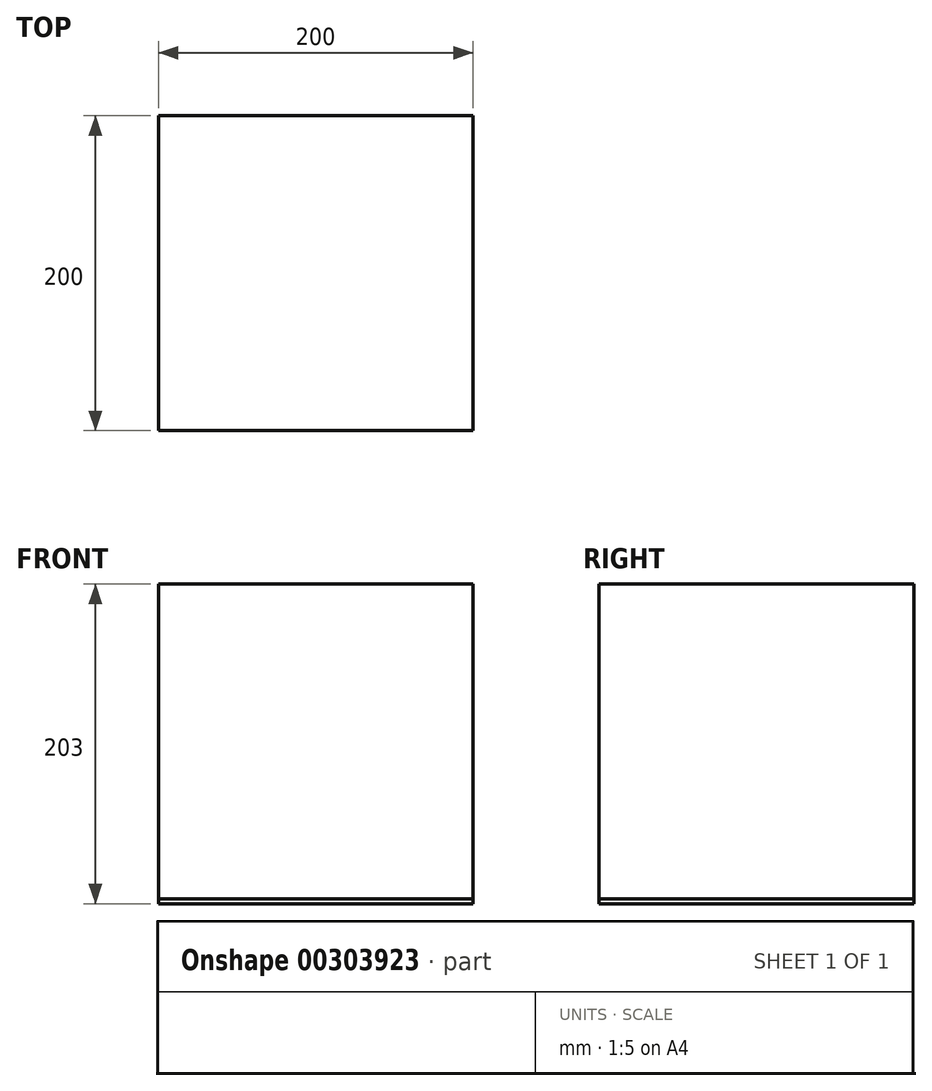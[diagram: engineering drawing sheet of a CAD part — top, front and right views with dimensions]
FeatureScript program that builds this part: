
annotation { "Feature Type Name" : "Feature", "Feature Type Description" : "" }
export const myFeature = defineFeature(function(context is Context, id is Id, definition is map)
    precondition{}
    {
        {
            var Q0;
            Q0=qCreatedBy(makeId("Top.planeOp"),FACE);
            var sketch = newSketch(context, id + "F0", { "sketchPlane" : qUnion([Q0])});
            skLineSegment(sketch, "E0.bottom", {"start": v(-100, 100) * mm, "end": v(100, 100) * mm});
            skLineSegment(sketch, "E0.top", {"start": v(-100, -100) * mm, "end": v(100, -100) * mm});
            skLineSegment(sketch, "E0.left", {"start": v(-100, 100) * mm, "end": v(-100, -100) * mm});
            skLineSegment(sketch, "E0.right", {"start": v(100, 100) * mm, "end": v(100, -100) * mm});
            skPoint(sketch, "E0.middle", {"position": v(0, 0) * mm});
            skSolve(sketch);
        }
        {
            var Q0;
            Q0=makeQuery(id+"F0.imprint","IMPRINT",FACE,{"disambiguationData":[TD([[makeQuery(id+"F0.imprint","IMPRINT",EDGE,{"derivedFrom":sQuery(id+"F0.wireOp",EDGE,"E0.bottom")}),-1.0]])]});
            extrude(context, id + "F1", {"entities" : qUnion([Q0]), "oppositeDirection" : true, "depth" : 3 * mm});
        }
        {
            var Q0;
            Q0=makeQuery(id+"F1.opExtrude","CAP_FACE",FACE,{"disambiguationData":[OSD([sQuery(id+"F0.wireOp",EDGE,"E0.bottom"),sQuery(id+"F0.wireOp",EDGE,"E0.top"),sQuery(id+"F0.wireOp",EDGE,"E0.left"),sQuery(id+"F0.wireOp",EDGE,"E0.right")])],"isStart":true});
            extrude(context, id + "F2", {"entities" : qUnion([Q0]), "depth" : 200 * mm});
        }
    });
